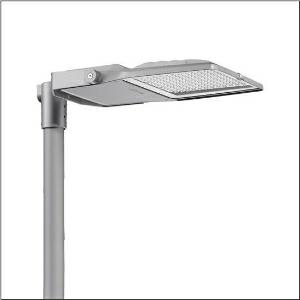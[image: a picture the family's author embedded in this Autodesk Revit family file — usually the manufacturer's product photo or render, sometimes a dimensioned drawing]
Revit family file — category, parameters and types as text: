
# Revit family: floodlight_fl_21_midi___pl43_5xa7786f2a3a_0f3f
name_source: partatom
category: Lighting Fixtures
units: mm (PartAtom-declared; Revit-internal decimal feet)

## family parameters
Cut with Voids When Loaded = No
Host = Face
Light Source = No
Part Type = Normal
Room Calculation Point = No
Round Connector Dimension = Use Diameter
Shared = No

## types (1)
- --- (1 x LED, 36680 lm, 271.6 W, 3000K)
    Apparent Load = 272 VA
    CIE Flux Codes = 27 78 99 100 100
    Color Rendering = 70
    Color Temperature = 3000K
    Default Elevation = 1800 mm
    Description = Floodlight FL 21 midi, floodlight, primary light control with lens, of PMMA, primary optical cover: protective disc, of toughened safety glass, transparent, light distribution: PL43, light emission: direct distribution, installation type: surface-mounted, LED, High Power LED, rated luminous flux: 36.680lm, luminous efficacy: 135lm/W, light colour: 730, colour temperature: 3000K, control gear: Smart Interface (Zhaga), control: flexible luminous flux parameterisation, time-dependent luminous flux control, constant luminous flux control, overheat protection, pre-setting: logarithmic dimming characteristic, with terminal, 6-pole, mains connection: 220..240V, AC, 50/60Hz, start of lifetime: 272W, end of service life: 287W, reduction: 123W, luminaire housing, of diecast aluminium, powder-coated, Siteco® metallic grey (DB 702S), corrosivity category C5 mid according to DIN EN ISO 12944, suitable for swimming pools, chlorine-resistant, sealing non-destructively replaceable, please order mast flange separately, mast bracket, of steel, galvanised, powder-coated, Siteco® metallic grey (DB 702S), Smart Interface below and above, protection rating (complete): IP66, insulation class (complete): insulation class II (safety insulation), certification: CE, ENEC, VDE, protection symbol: D, impact resistance: IK08, permissible operating ambient temperature: -40..+40°C, permissible operating ambient temperature for outdoor applications: -40..+50°C, standard: DIN EN 12944, LABS conformity tested according to VDMA 24364:2018-05, packaging unit: 1 piece

Light Distribution: PL43
    Height = 76 mm
    Lamp = 1 x LED
    Lamp Light Flux = 36680 lm
    Lamp Power = 271.6 W
    Lamp count = 1
    Length = 657 mm
    Luminous efficacy = 135 lm/W
    Manufacturer = Siteco
    ModVariant = No
    Model = 5XA7786F2A3A
    Number of Poles = 1
    OnlyDefault = Yes
    Power Factor = 1
    Product Name = Floodlight FL 21 midi | PL43
    Product group = floodlight | pylon annexe
    ProductGroupID = 6201
    Protection Class = Protection class II
    Protection Degree = IP 66
    RLX_Detail_Level = 1
    RLX_Emergency_Light_Flux = 0 lm
    RLX_Emergency_Type = 0
    RLX_Emergency_Type_DB = No
    RlxData = <blob elided: 153485 chars, md5=2334dea7>
    Socket = socket
    Standby Power = 0 W
    System Light Flux = 36680 lm
    System Power = 272 W
    Type Comments = factory setting: luminous flux: 100 % | dim-lin: 254 | 620 mA
    Type Image = l_1007123.jpg
    URL = http://relux.com
    VarID = @adj_198567
    Voltage = 0 V
    Weight = 0.00 kg
    Width = 442 mm

## geometry (parser evidence)
native form markers: Blend x4, Sweep x14
no freeform markers — native parametric forms only
